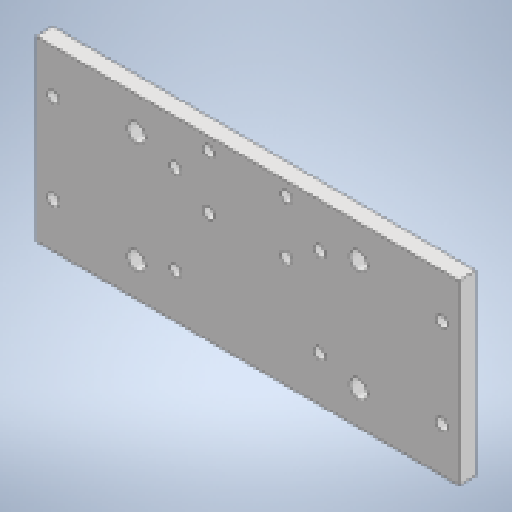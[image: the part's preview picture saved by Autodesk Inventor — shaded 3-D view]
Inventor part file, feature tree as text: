
AUTODESK INVENTOR PART (.ipt)
format: ipt  version: 2023 (Build 270158000, 158)  size: 168,448 bytes
history: native  units: mm
features: extrude x4, sketch x4
ambient origin geometry x8: Origin, YZ Plane, XZ Plane, XY Plane, X Axis, Y Axis, Z Axis, Center Point
bodies: Solid1 (feature_tree)
feature tree (8):
  extrude  "Extrusion1"  Depth=190.5mm
  extrude  "Extrusion2"  Depth=7.62mm
  extrude  "Extrusion3"  Depth=8.0mm
  extrude  "Extrusion4"  Depth=10.0mm
  sketch  "Sketch1"  dims[d0=80.0mm d1=190.5mm]
  sketch  "Sketch2"  dims[d2=7.62mm d3=0.0mm d4=100.0mm]
  sketch  "Sketch3"  dims[d5=50.0mm d6=8.0mm]
  sketch  "Sketch4"  dims[d7=7.62mm d8=0.0mm d9=5.0mm d10=55.0mm d11=40.0mm d12=60.0mm d13=10.0mm d14=0.0mm d15=5.0mm d16=35.0mm d17=24.0mm d18=6.0mm d19=10.0mm d20=0.0mm]
